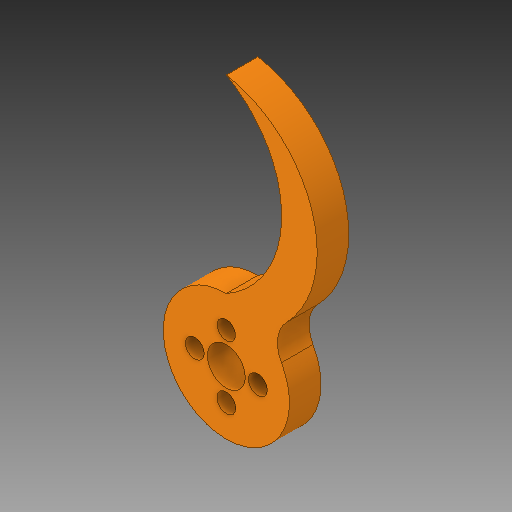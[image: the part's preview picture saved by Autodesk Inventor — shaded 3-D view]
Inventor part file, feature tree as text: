
AUTODESK INVENTOR PART (.ipt)
format: ipt  version: 2019 (Build 230136000, 136)  size: 134,144 bytes
history: native  units: in
note: dims shown in document units (in); Inventor stores cm internally (conversion verified against a paired STEP export)
features: extrude x5, sketch x5, fillet x1
ambient origin geometry x8: Origin, YZ Plane, XZ Plane, XY Plane, X Axis, Y Axis, Z Axis, Center Point
bodies: Solid1 (feature_tree)
feature tree (11):
  extrude  "Extrusion1"  Depth=0.25in TaperAngle=0.0deg
  extrude  "Extrusion2"  Depth=0.25in TaperAngle=0.0deg
  extrude  "Extrusion3"  Depth=0.25in
  extrude  "Extrusion4"  Depth=0.15in
  extrude  "Extrusion5"  Depth=0.15in
  fillet  "Fillet1"  Radius=0.25in
  sketch  "Sketch1"  dims[d0=1.0in d1=0.25in d2=0.0in]
  sketch  "Sketch2"  dims[d3=0.3in d4=0.25in d5=0.0in]
  sketch  "Sketch3"  dims[d6=0.145in d7=0.25in]
  sketch  "Sketch4"  dims[d8=0.25in d9=0.0in d10=0.15in]
  sketch  "Sketch5"  dims[d11=0.15in d12=0.15in d13=0.25in d14=0.25in d15=0.25in d16=0.25in d17=0.0in d18=1.5in d19=90.0deg d20=0.25in d21=0.0in d22=0.25in]
